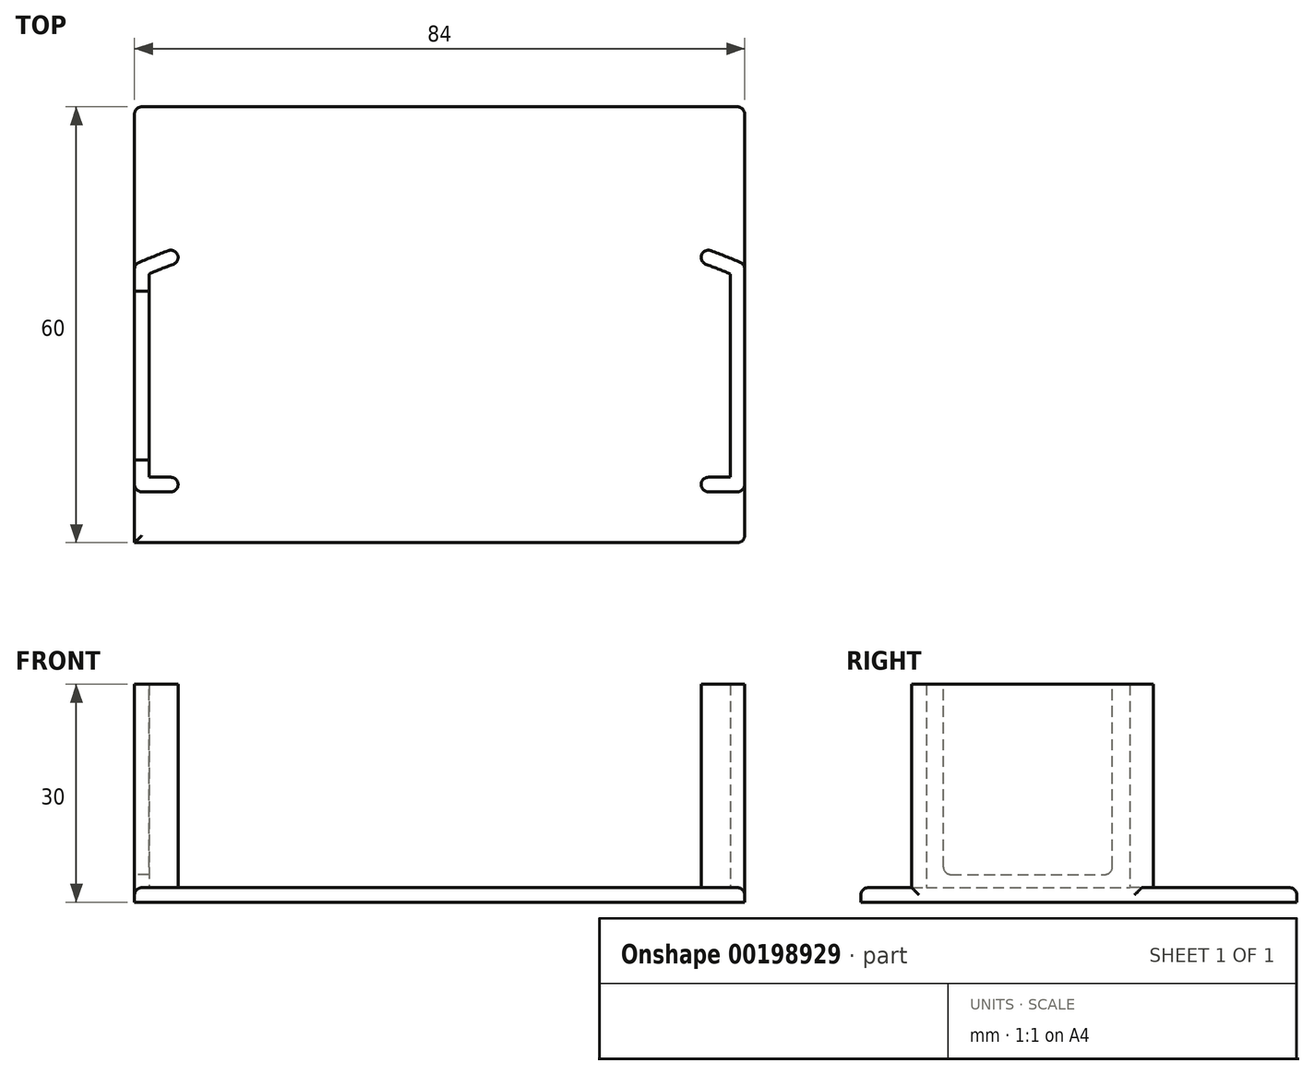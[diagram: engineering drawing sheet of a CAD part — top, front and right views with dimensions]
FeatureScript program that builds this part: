
annotation { "Feature Type Name" : "Feature", "Feature Type Description" : "" }
export const myFeature = defineFeature(function(context is Context, id is Id, definition is map)
    precondition{}
    {
        {
            var Q0;
            Q0=qCreatedBy(makeId("Top.planeOp"),FACE);
            var sketch = newSketch(context, id + "F0", { "sketchPlane" : qUnion([Q0])});
            skLineSegment(sketch, "E0.bottom", {"start": v(40, -14) * mm, "end": v(-40, -14) * mm});
            skLineSegment(sketch, "E0.top", {"start": v(40, 14) * mm, "end": v(-40, 14) * mm});
            skLineSegment(sketch, "E0.left", {"start": v(40, -14) * mm, "end": v(40, 14) * mm});
            skLineSegment(sketch, "E0.right", {"start": v(-40, -14) * mm, "end": v(-40, 14) * mm});
            skPoint(sketch, "E0.middle", {"position": v(0, 0) * mm});
            skArc(sketch, "E1", {"start": v(40, 14) * mm, "mid": v(0, 22) * mm, "end": v(-40, 14) * mm});
            skArc(sketch, "E2.0", {"start": v(42, 15.32) * mm, "mid": v(0, 24) * mm, "end": v(-42, 15.32) * mm});
            skLineSegment(sketch, "E2.1", {"start": v(42, -16) * mm, "end": v(42, 15.32) * mm});
            skLineSegment(sketch, "E2.2", {"start": v(42, -16) * mm, "end": v(-42, -16) * mm});
            skLineSegment(sketch, "E2.3", {"start": v(-42, -16) * mm, "end": v(-42, 15.32) * mm});
            skLineSegment(sketch, "E3", {"start": v(-36, -16) * mm, "end": v(-36, -14) * mm});
            skLineSegment(sketch, "E4", {"start": v(36, -16) * mm, "end": v(36, -14) * mm});
            skLineSegment(sketch, "E5", {"start": v(36, 15.57) * mm, "end": v(36, 17.7) * mm});
            skLineSegment(sketch, "E6", {"start": v(-36, 15.57) * mm, "end": v(-36, 17.7) * mm});
            skLineSegment(sketch, "E7.bottom", {"start": v(42, -23) * mm, "end": v(-42, -23) * mm});
            skLineSegment(sketch, "E7.top", {"start": v(42, 37) * mm, "end": v(-42, 37) * mm});
            skLineSegment(sketch, "E7.left", {"start": v(42, -23) * mm, "end": v(42, 37) * mm});
            skLineSegment(sketch, "E7.right", {"start": v(-42, -23) * mm, "end": v(-42, 37) * mm});
            skSolve(sketch);
        }
        {
            var Q0;
            {var subQ0=sQuery(id+"F0.wireOp",EDGE,"E5");Q0=makeQuery(id+"F0.imprint","IMPRINT",FACE,{"disambiguationData":[TD([[makeQuery(id+"F0.imprint","IMPRINT",EDGE,{"derivedFrom":subQ0}),1.0]])]});}
            var Q1;
            {var subQ0=sQuery(id+"F0.wireOp",EDGE,"E0.top");Q1=makeQuery(id+"F0.imprint","IMPRINT",FACE,{"disambiguationData":[TD([[makeQuery(id+"F0.imprint","IMPRINT",EDGE,{"derivedFrom":subQ0}),-1.0]])]});}
            var Q2;
            Q2=makeQuery(id+"F0.imprint","IMPRINT",FACE,{"disambiguationData":[TD([[makeQuery(id+"F0.imprint","IMPRINT",EDGE,{"derivedFrom":sQuery(id+"F0.wireOp",EDGE,"E0.top")}),1.0]])]});
            var Q3;
            {var subQ0=sQuery(id+"F0.wireOp",EDGE,"E3");Q3=makeQuery(id+"F0.imprint","IMPRINT",FACE,{"disambiguationData":[TD([[makeQuery(id+"F0.imprint","IMPRINT",EDGE,{"derivedFrom":subQ0}),-1.0]])]});}
            var Q4;
            {var subQ0=sQuery(id+"F0.wireOp",EDGE,"E7.top");Q4=makeQuery(id+"F0.imprint","IMPRINT",FACE,{"disambiguationData":[TD([[makeQuery(id+"F0.imprint","IMPRINT",EDGE,{"derivedFrom":subQ0}),1.0]])]});}
            var Q5;
            {var subQ0=sQuery(id+"F0.wireOp",EDGE,"E7.bottom");Q5=makeQuery(id+"F0.imprint","IMPRINT",FACE,{"disambiguationData":[TD([[makeQuery(id+"F0.imprint","IMPRINT",EDGE,{"derivedFrom":subQ0}),-1.0]])]});}
            extrude(context, id + "F1", {"entities" : qUnion([Q0, Q1, Q2, Q3, Q4, Q5]), "depth" : 2 * mm});
        }
        {
            var Q0;
            {var subQ5=sQuery(id+"F0.wireOp",EDGE,"E0.right");Q0=makeQuery(id+"F0.imprint","IMPRINT",FACE,{"disambiguationData":[TD([[makeQuery(id+"F0.imprint","IMPRINT",EDGE,{"derivedFrom":subQ5}),1.0]])]});}
            var Q1;
            {var subQ7=sQuery(id+"F0.wireOp",EDGE,"E0.left");Q1=makeQuery(id+"F0.imprint","IMPRINT",FACE,{"disambiguationData":[TD([[makeQuery(id+"F0.imprint","IMPRINT",EDGE,{"derivedFrom":subQ7}),-1.0]])]});}
            extrude(context, id + "F2", {"entities" : qUnion([Q0, Q1]), "operationType" : NewBodyOperationType.ADD, "depth" : 30 * mm});
        }
        {
            var Q0;
            {var subQ0=sQuery(id+"F0.wireOp",EDGE,"E7.right");Q0=makeQuery(id+"F2.boolean.opBoolean","MERGE",FACE,{"derivedFrom":[makeQuery(id+"F1.opExtrude","SWEPT_FACE",FACE,{"disambiguationData":[OSD([subQ0]),TDD([makeQuery(id+"F0.imprint","IMPRINT",EDGE,{"disambiguationData":[TD([[makeQuery(id+"F0.imprint","INTERSECT",VERTEX,{"derivedFrom":[sQuery(id+"F0.wireOp",EDGE,"E2.2"),subQ0]}),1.0]])],"derivedFrom":subQ0})])]}),makeQuery(id+"F1.opExtrude","SWEPT_FACE",FACE,{"disambiguationData":[OSD([subQ0]),TDD([makeQuery(id+"F0.imprint","IMPRINT",EDGE,{"disambiguationData":[TD([[makeQuery(id+"F0.imprint","INTERSECT",VERTEX,{"derivedFrom":[sQuery(id+"F0.wireOp",EDGE,"E2.0"),subQ0]}),-1.0]])],"derivedFrom":subQ0})])]}),makeQuery(id+"F2.opExtrude","SWEPT_FACE",FACE,{"disambiguationData":[OSD([subQ0])]})]});}
            var sketch = newSketch(context, id + "F3", { "sketchPlane" : qUnion([Q0])});
            skLineSegment(sketch, "E8.bottom", {"start": v(-11.6, 30) * mm, "end": v(11.63, 30) * mm});
            skLineSegment(sketch, "E8.top", {"start": v(-11.6, 3.82) * mm, "end": v(11.63, 3.82) * mm});
            skLineSegment(sketch, "E8.left", {"start": v(-11.6, 30) * mm, "end": v(-11.6, 3.82) * mm});
            skLineSegment(sketch, "E8.right", {"start": v(11.63, 30) * mm, "end": v(11.63, 3.82) * mm});
            skSolve(sketch);
        }
        {
            var Q0;
            Q0=makeQuery(id+"F3.imprint","IMPRINT",FACE,{"disambiguationData":[TD([[makeQuery(id+"F3.imprint","IMPRINT",EDGE,{"derivedFrom":sQuery(id+"F3.wireOp",EDGE,"E8.bottom")}),1.0]])]});
            extrude(context, id + "F4", {"entities" : qUnion([Q0]), "operationType" : NewBodyOperationType.REMOVE, "endBound" : BoundingType.UP_TO_NEXT, "oppositeDirection" : true, "depth" : 25 * mm});
        }
        {
            var Q0;
            Q0=makeQuery(id+"F1.opExtrude","CAP_EDGE",EDGE,{"disambiguationData":[OSD([sQuery(id+"F0.wireOp",EDGE,"E7.bottom")])],"isStart":false});
            var Q1;
            Q1=makeQuery(id+"F1.opExtrude","SWEPT_EDGE",EDGE,{"disambiguationData":[OSD([sQuery(id+"F0.wireOp",EDGE,"E7.bottom"),sQuery(id+"F0.wireOp",EDGE,"E7.left")])]});
            var Q2;
            {var subQ0=sQuery(id+"F0.wireOp",EDGE,"E7.left");Q2=makeQuery(id+"F1.opExtrude","CAP_EDGE",EDGE,{"disambiguationData":[OSD([subQ0]),TDD([makeQuery(id+"F0.imprint","IMPRINT",EDGE,{"disambiguationData":[TD([[makeQuery(id+"F0.imprint","INTERSECT",VERTEX,{"derivedFrom":[sQuery(id+"F0.wireOp",EDGE,"E2.2"),subQ0]}),1.0]])],"derivedFrom":subQ0})])],"isStart":false});}
            var Q3;
            {var subQ0=sQuery(id+"F0.wireOp",EDGE,"E7.right");Q3=makeQuery(id+"F1.opExtrude","CAP_EDGE",EDGE,{"disambiguationData":[OSD([subQ0]),TDD([makeQuery(id+"F0.imprint","IMPRINT",EDGE,{"disambiguationData":[TD([[makeQuery(id+"F0.imprint","INTERSECT",VERTEX,{"derivedFrom":[sQuery(id+"F0.wireOp",EDGE,"E2.2"),subQ0]}),1.0]])],"derivedFrom":subQ0})])],"isStart":false});}
            var Q4;
            {var subQ0=sQuery(id+"F0.wireOp",EDGE,"E7.right");Q4=makeQuery(id+"F1.opExtrude","CAP_EDGE",EDGE,{"disambiguationData":[OSD([subQ0]),TDD([makeQuery(id+"F0.imprint","IMPRINT",EDGE,{"disambiguationData":[TD([[makeQuery(id+"F0.imprint","INTERSECT",VERTEX,{"derivedFrom":[sQuery(id+"F0.wireOp",EDGE,"E2.0"),subQ0]}),-1.0]])],"derivedFrom":subQ0})])],"isStart":false});}
            var Q5;
            Q5=makeQuery(id+"F1.opExtrude","CAP_EDGE",EDGE,{"disambiguationData":[OSD([sQuery(id+"F0.wireOp",EDGE,"E7.top")])],"isStart":false});
            var Q6;
            Q6=makeQuery(id+"F1.opExtrude","SWEPT_EDGE",EDGE,{"disambiguationData":[OSD([sQuery(id+"F0.wireOp",EDGE,"E7.top"),sQuery(id+"F0.wireOp",EDGE,"E7.right")])]});
            var Q7;
            {var subQ0=sQuery(id+"F0.wireOp",EDGE,"E7.left");Q7=makeQuery(id+"F1.opExtrude","CAP_EDGE",EDGE,{"disambiguationData":[OSD([subQ0]),TDD([makeQuery(id+"F0.imprint","IMPRINT",EDGE,{"disambiguationData":[TD([[makeQuery(id+"F0.imprint","INTERSECT",VERTEX,{"derivedFrom":[sQuery(id+"F0.wireOp",EDGE,"E2.0"),subQ0]}),-1.0]])],"derivedFrom":subQ0})])],"isStart":false});}
            var Q8;
            Q8=makeQuery(id+"F1.opExtrude","SWEPT_EDGE",EDGE,{"disambiguationData":[OSD([sQuery(id+"F0.wireOp",EDGE,"E7.top"),sQuery(id+"F0.wireOp",EDGE,"E7.left")])]});
            var Q9;
            Q9=makeQuery(id+"F2.opExtrude","SWEPT_EDGE",EDGE,{"disambiguationData":[OSD([sQuery(id+"F0.wireOp",EDGE,"E2.0"),sQuery(id+"F0.wireOp",EDGE,"E7.left")])]});
            var Q10;
            Q10=makeQuery(id+"F2.opExtrude","SWEPT_EDGE",EDGE,{"disambiguationData":[OSD([sQuery(id+"F0.wireOp",EDGE,"E2.2"),sQuery(id+"F0.wireOp",EDGE,"E7.left")])]});
            var Q11;
            Q11=makeQuery(id+"F2.opExtrude","SWEPT_EDGE",EDGE,{"disambiguationData":[OSD([sQuery(id+"F0.wireOp",EDGE,"E2.0"),sQuery(id+"F0.wireOp",EDGE,"E5")])]});
            var Q12;
            Q12=makeQuery(id+"F2.opExtrude","SWEPT_EDGE",EDGE,{"disambiguationData":[OSD([sQuery(id+"F0.wireOp",EDGE,"E1"),sQuery(id+"F0.wireOp",EDGE,"E5")])]});
            var Q13;
            Q13=makeQuery(id+"F2.opExtrude","SWEPT_EDGE",EDGE,{"disambiguationData":[OSD([sQuery(id+"F0.wireOp",EDGE,"E2.2"),sQuery(id+"F0.wireOp",EDGE,"E4")])]});
            var Q14;
            Q14=makeQuery(id+"F2.opExtrude","SWEPT_EDGE",EDGE,{"disambiguationData":[OSD([sQuery(id+"F0.wireOp",EDGE,"E0.bottom"),sQuery(id+"F0.wireOp",EDGE,"E4")])]});
            var Q15;
            Q15=makeQuery(id+"F2.opExtrude","SWEPT_EDGE",EDGE,{"disambiguationData":[OSD([sQuery(id+"F0.wireOp",EDGE,"E2.0"),sQuery(id+"F0.wireOp",EDGE,"E7.right")])]});
            var Q16;
            Q16=makeQuery(id+"F2.opExtrude","SWEPT_EDGE",EDGE,{"disambiguationData":[OSD([sQuery(id+"F0.wireOp",EDGE,"E2.0"),sQuery(id+"F0.wireOp",EDGE,"E6")])]});
            var Q17;
            Q17=makeQuery(id+"F4.boolean.opBoolean","COPY",EDGE,{"derivedFrom":makeQuery(id+"F4.opExtrude","CAP_EDGE",EDGE,{"disambiguationData":[OSD([sQuery(id+"F3.wireOp",EDGE,"E8.left")])],"isStart":true})});
            var Q18;
            Q18=makeQuery(id+"F4.boolean.opBoolean","COPY",EDGE,{"derivedFrom":makeQuery(id+"F4.opExtrude","CAP_EDGE",EDGE,{"disambiguationData":[OSD([sQuery(id+"F3.wireOp",EDGE,"E8.right")])],"isStart":true})});
            var Q19;
            Q19=makeQuery(id+"F2.opExtrude","SWEPT_EDGE",EDGE,{"disambiguationData":[OSD([sQuery(id+"F0.wireOp",EDGE,"E2.2"),sQuery(id+"F0.wireOp",EDGE,"E7.right")])]});
            var Q20;
            Q20=makeQuery(id+"F2.opExtrude","SWEPT_EDGE",EDGE,{"disambiguationData":[OSD([sQuery(id+"F0.wireOp",EDGE,"E2.2"),sQuery(id+"F0.wireOp",EDGE,"E3")])]});
            var Q21;
            Q21=makeQuery(id+"F2.opExtrude","SWEPT_EDGE",EDGE,{"disambiguationData":[OSD([sQuery(id+"F0.wireOp",EDGE,"E0.bottom"),sQuery(id+"F0.wireOp",EDGE,"E3")])]});
            var Q22;
            Q22=makeQuery(id+"F2.opExtrude","SWEPT_EDGE",EDGE,{"disambiguationData":[OSD([sQuery(id+"F0.wireOp",EDGE,"E1"),sQuery(id+"F0.wireOp",EDGE,"E6")])]});
            var Q23;
            Q23=makeQuery(id+"F4.boolean.opBoolean","COPY",EDGE,{"derivedFrom":makeQuery(id+"F4.opExtrude","CAP_EDGE",EDGE,{"disambiguationData":[OSD([sQuery(id+"F3.wireOp",EDGE,"E8.right")])],"isStart":false})});
            var Q24;
            Q24=makeQuery(id+"F4.boolean.opBoolean","COPY",EDGE,{"derivedFrom":makeQuery(id+"F4.opExtrude","CAP_EDGE",EDGE,{"disambiguationData":[OSD([sQuery(id+"F3.wireOp",EDGE,"E8.left")])],"isStart":false})});
            var Q25;
            Q25=makeQuery(id+"F4.boolean.opBoolean","COPY",EDGE,{"derivedFrom":makeQuery(id+"F4.opExtrude","CAP_EDGE",EDGE,{"disambiguationData":[OSD([sQuery(id+"F3.wireOp",EDGE,"E8.top")])],"isStart":true})});
            var Q26;
            Q26=makeQuery(id+"F4.boolean.opBoolean","COPY",EDGE,{"derivedFrom":makeQuery(id+"F4.opExtrude","CAP_EDGE",EDGE,{"disambiguationData":[OSD([sQuery(id+"F3.wireOp",EDGE,"E8.top")])],"isStart":false})});
            var Q27;
            Q27=makeQuery(id+"F4.boolean.opBoolean","COPY",EDGE,{"derivedFrom":makeQuery(id+"F4.opExtrude","SWEPT_EDGE",EDGE,{"disambiguationData":[OSD([sQuery(id+"F3.wireOp",EDGE,"E8.top"),sQuery(id+"F3.wireOp",EDGE,"E8.right")])]})});
            var Q28;
            Q28=makeQuery(id+"F4.boolean.opBoolean","COPY",EDGE,{"derivedFrom":makeQuery(id+"F4.opExtrude","SWEPT_EDGE",EDGE,{"disambiguationData":[OSD([sQuery(id+"F3.wireOp",EDGE,"E8.top"),sQuery(id+"F3.wireOp",EDGE,"E8.left")])]})});
            fillet(context, id + "F5", {"entities" : qUnion([Q0, Q1, Q2, Q3, Q4, Q5, Q6, Q7, Q8, Q9, Q10, Q11, Q12, Q13, Q14, Q15, Q16, Q17, Q18, Q19, Q20, Q21, Q22, Q23, Q24, Q25, Q26, Q27, Q28]), "radius" : 1 * mm, "tangentPropagation" : true, "allowEdgeOverflow" : false});
        }
    });
